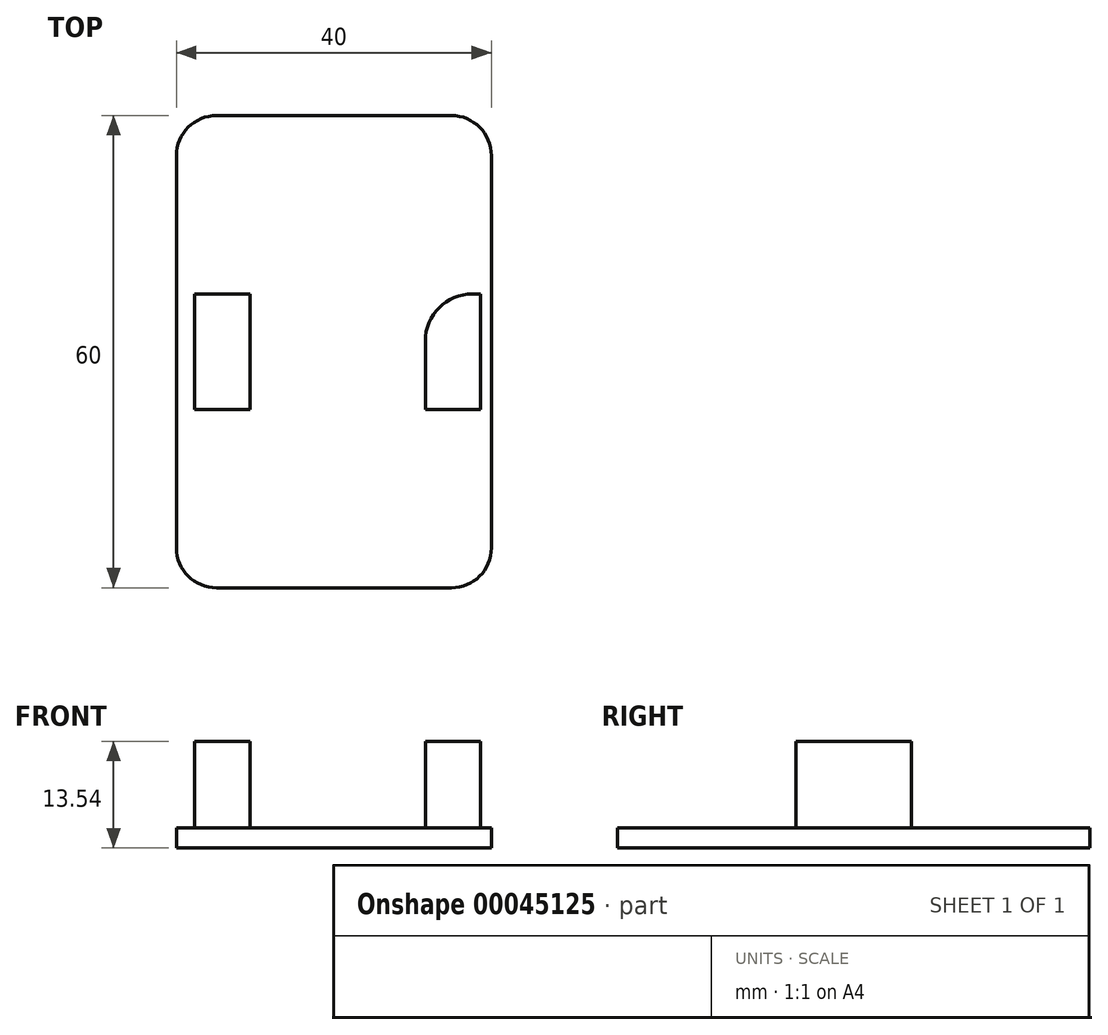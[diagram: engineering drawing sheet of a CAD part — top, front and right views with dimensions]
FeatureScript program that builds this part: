
annotation { "Feature Type Name" : "Feature", "Feature Type Description" : "" }
export const myFeature = defineFeature(function(context is Context, id is Id, definition is map)
    precondition{}
    {
        {
            var Q0;
            Q0=qCreatedBy(makeId("Top.planeOp"),FACE);
            var sketch = newSketch(context, id + "F0", { "sketchPlane" : qUnion([Q0])});
            skLineSegment(sketch, "E0.rect.bottom", {"start": v(20, 30) * mm, "end": v(-20, 30) * mm});
            skLineSegment(sketch, "E0.rect.top", {"start": v(20, -30) * mm, "end": v(-20, -30) * mm});
            skLineSegment(sketch, "E0.rect.left", {"start": v(20, 30) * mm, "end": v(20, -30) * mm});
            skLineSegment(sketch, "E0.rect.right", {"start": v(-20, 30) * mm, "end": v(-20, -30) * mm});
            skPoint(sketch, "E0.rect.middle", {"position": v(0, 0) * mm});
            skSolve(sketch);
        }
        {
            var Q0;
            Q0 = qSketchRegion(id + "F0", true);
            extrude(context, id + "F1", {"entities" : qUnion([Q0]), "depth" : 2.54 * mm});
        }
        {
            var Q0;
            Q0=makeQuery(id+"F1.opExtrude","SWEPT_EDGE",EDGE,{"disambiguationData":[OSD([sQuery(id+"F0.wireOp",EDGE,"E0.rect.top"),sQuery(id+"F0.wireOp",EDGE,"E0.rect.right")])]});
            var Q1;
            Q1=makeQuery(id+"F1.opExtrude","SWEPT_EDGE",EDGE,{"disambiguationData":[OSD([sQuery(id+"F0.wireOp",EDGE,"E0.rect.top"),sQuery(id+"F0.wireOp",EDGE,"E0.rect.left")])]});
            var Q2;
            Q2=makeQuery(id+"F1.opExtrude","SWEPT_EDGE",EDGE,{"disambiguationData":[OSD([sQuery(id+"F0.wireOp",EDGE,"E0.rect.bottom"),sQuery(id+"F0.wireOp",EDGE,"E0.rect.right")])]});
            var Q3;
            Q3=makeQuery(id+"F1.opExtrude","SWEPT_EDGE",EDGE,{"disambiguationData":[OSD([sQuery(id+"F0.wireOp",EDGE,"E0.rect.bottom"),sQuery(id+"F0.wireOp",EDGE,"E0.rect.left")])]});
            fillet(context, id + "F2", {"entities" : qUnion([Q0, Q1, Q2, Q3]), "radius" : 5.08 * mm, "tangentPropagation" : true, "allowEdgeOverflow" : false});
        }
        {
            var Q0;
            Q0=makeQuery(id+"F1.opExtrude","CAP_FACE",FACE,{"disambiguationData":[OSD([sQuery(id+"F0.wireOp",EDGE,"E0.rect.bottom"),sQuery(id+"F0.wireOp",EDGE,"E0.rect.top"),sQuery(id+"F0.wireOp",EDGE,"E0.rect.left"),sQuery(id+"F0.wireOp",EDGE,"E0.rect.right")])],"isStart":false});
            var sketch = newSketch(context, id + "F3", { "sketchPlane" : qUnion([Q0])});
            skPoint(sketch, "E1.rect.middle", {"position": v(0, 0) * mm});
            skLineSegment(sketch, "E2.bottom", {"start": v(-10.68, -7.33) * mm, "end": v(-17.68, -7.33) * mm});
            skLineSegment(sketch, "E2.top", {"start": v(-10.68, 7.33) * mm, "end": v(-17.68, 7.33) * mm});
            skLineSegment(sketch, "E2.left", {"start": v(-10.68, -7.33) * mm, "end": v(-10.68, 7.33) * mm});
            skLineSegment(sketch, "E2.right", {"start": v(-17.68, -7.33) * mm, "end": v(-17.68, 7.33) * mm});
            skLineSegment(sketch, "E3.bottom", {"start": v(11.6, -7.33) * mm, "end": v(18.6, -7.33) * mm});
            skLineSegment(sketch, "E3.top", {"start": v(11.6, 7.33) * mm, "end": v(18.6, 7.33) * mm});
            skLineSegment(sketch, "E3.left", {"start": v(11.6, -7.33) * mm, "end": v(11.6, 7.33) * mm});
            skLineSegment(sketch, "E3.right", {"start": v(18.6, -7.33) * mm, "end": v(18.6, 7.33) * mm});
            skLineSegment(sketch, "E4", {"start": v(-11.6, 7.33) * mm, "end": v(10.68, 7.33) * mm});
            skSolve(sketch);
        }
        {
            var Q0;
            Q0 = qSketchRegion(id + "F3", true);
            extrude(context, id + "F4", {"entities" : qUnion([Q0]), "operationType" : NewBodyOperationType.ADD, "depth" : 11 * mm});
        }
        {
            var Q0;
            Q0=makeQuery(id+"F4.opExtrude","SWEPT_EDGE",EDGE,{"disambiguationData":[OSD([sQuery(id+"F3.wireOp",EDGE,"E3.top"),sQuery(id+"F3.wireOp",EDGE,"E3.left")])]});
            fillet(context, id + "F5", {"entities" : qUnion([Q0]), "radius" : 6 * mm, "tangentPropagation" : true, "allowEdgeOverflow" : false});
        }
    });
